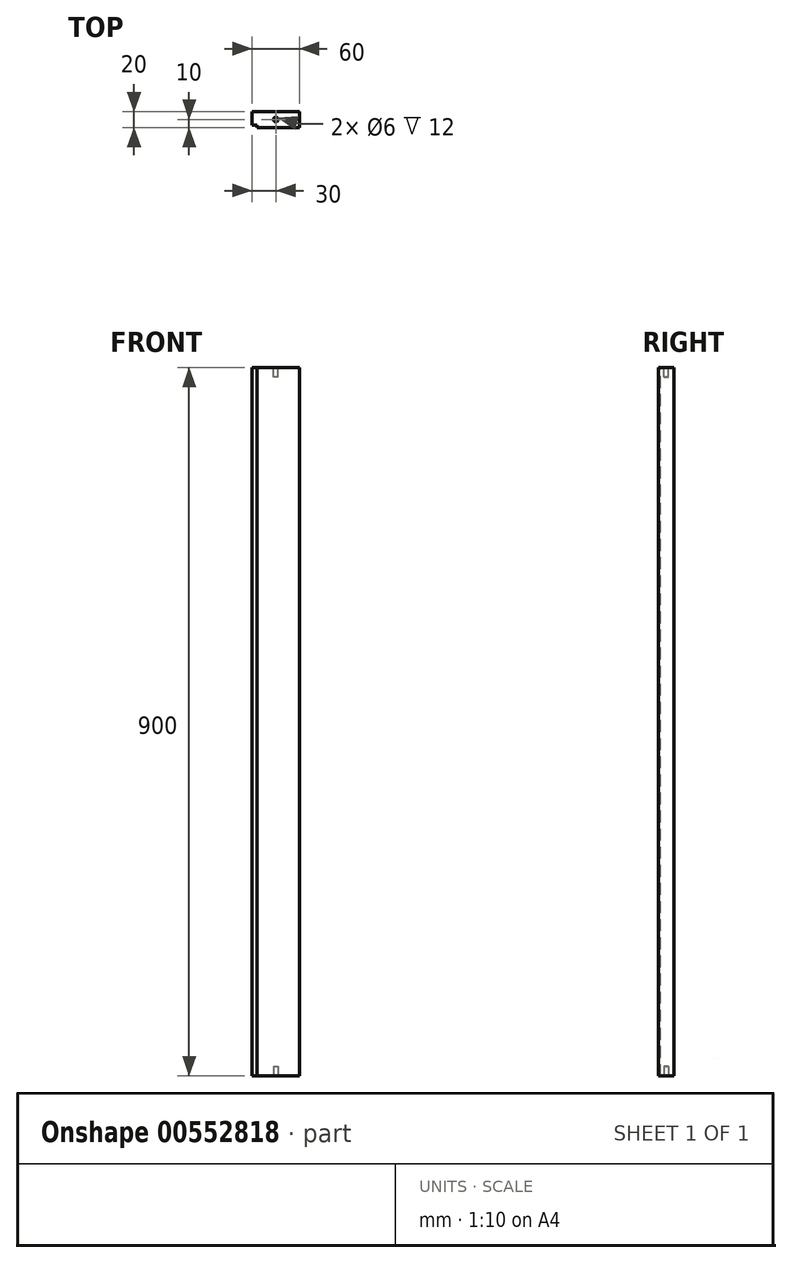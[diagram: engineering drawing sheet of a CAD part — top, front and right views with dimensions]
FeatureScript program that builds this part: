
annotation { "Feature Type Name" : "Feature", "Feature Type Description" : "" }
export const myFeature = defineFeature(function(context is Context, id is Id, definition is map)
    precondition{}
    {
        {
            var Q0;
            Q0=qCreatedBy(makeId("Top.planeOp"),FACE);
            var sketch = newSketch(context, id + "F0", { "sketchPlane" : qUnion([Q0])});
            skLineSegment(sketch, "E0.bottom", {"start": v(0, 0) * mm, "end": v(60, 0) * mm});
            skLineSegment(sketch, "E0.top", {"start": v(0, 20) * mm, "end": v(60, 20) * mm});
            skLineSegment(sketch, "E0.left", {"start": v(0, 0) * mm, "end": v(0, 20) * mm});
            skLineSegment(sketch, "E0.right", {"start": v(60, 0) * mm, "end": v(60, 20) * mm});
            skSolve(sketch);
        }
        {
            var Q0;
            Q0 = qSketchRegion(id + "F0", true);
            extrude(context, id + "F1", {"entities" : qUnion([Q0]), "depth" : 900 * mm, "offsetDistance" : 25 * mm});
        }
        {
            var Q0;
            Q0=makeQuery(id+"F1.opExtrude","CAP_FACE",FACE,{"disambiguationData":[OSD([sQuery(id+"F0.wireOp",EDGE,"E0.bottom"),sQuery(id+"F0.wireOp",EDGE,"E0.top"),sQuery(id+"F0.wireOp",EDGE,"E0.left"),sQuery(id+"F0.wireOp",EDGE,"E0.right")])],"isStart":false});
            var sketch = newSketch(context, id + "F2", { "sketchPlane" : qUnion([Q0])});
            skSolve(sketch);
        }
        {
            var Q0;
            Q0=makeQuery(id+"F1.opExtrude","CAP_FACE",FACE,{"disambiguationData":[OSD([sQuery(id+"F0.wireOp",EDGE,"E0.bottom"),sQuery(id+"F0.wireOp",EDGE,"E0.top"),sQuery(id+"F0.wireOp",EDGE,"E0.left"),sQuery(id+"F0.wireOp",EDGE,"E0.right")])],"isStart":true});
            var sketch = newSketch(context, id + "F3", { "sketchPlane" : qUnion([Q0])});
            skCircle(sketch, "E1", {"center": v(30, -10) * mm, "radius": 3 * mm});
            skPoint(sketch, "E1.centerSnap0", {"position": v(30, -20) * mm});
            skPoint(sketch, "E1.centerSnap1", {"position": v(60, -10) * mm});
            skSolve(sketch);
        }
        {
            var Q0;
            Q0=makeQuery(id+"F3.imprint","IMPRINT",FACE,{"disambiguationData":[TD([[makeQuery(id+"F3.imprint","IMPRINT",EDGE,{"derivedFrom":sQuery(id+"F3.wireOp",EDGE,"E1")}),1.0]])]});
            var Q1;
            Q1=sQuery(id+"F3.wireOp",EDGE,"E1");
            extrude(context, id + "F4", {"entities" : qUnion([Q0]), "operationType" : NewBodyOperationType.REMOVE, "surfaceEntities" : qUnion([Q1]), "oppositeDirection" : true, "depth" : 12 * mm, "offsetDistance" : 25 * mm});
        }
        {
            var Q0;
            Q0=makeQuery(id+"F2.imprint","IMPRINT",FACE,{"disambiguationData":[TD([[makeQuery(id+"F2.imprint","IMPRINT",EDGE,{"derivedFrom":makeQuery(id+"F1.opExtrude","CAP_EDGE",EDGE,{"disambiguationData":[OSD([sQuery(id+"F0.wireOp",EDGE,"E0.bottom")])],"isStart":false})}),1.0]])]});
            var sketch = newSketch(context, id + "F5", { "sketchPlane" : qUnion([Q0])});
            skCircle(sketch, "E2", {"center": v(30, 10) * mm, "radius": 3 * mm});
            skSolve(sketch);
        }
        {
            var Q0;
            Q0 = qSketchRegion(id + "F5", true);
            extrude(context, id + "F6", {"entities" : qUnion([Q0]), "operationType" : NewBodyOperationType.REMOVE, "oppositeDirection" : true, "depth" : 12 * mm, "offsetDistance" : 25 * mm});
        }
        {
            var Q0;
            Q0=makeQuery(id+"F2.imprint","IMPRINT",FACE,{"disambiguationData":[TD([[makeQuery(id+"F2.imprint","IMPRINT",EDGE,{"derivedFrom":makeQuery(id+"F1.opExtrude","CAP_EDGE",EDGE,{"disambiguationData":[OSD([sQuery(id+"F0.wireOp",EDGE,"E0.bottom")])],"isStart":false})}),1.0]])]});
            var sketch = newSketch(context, id + "F7", { "sketchPlane" : qUnion([Q0])});
            skLineSegment(sketch, "E3.bottom", {"start": v(0, 0) * mm, "end": v(6, 0) * mm});
            skLineSegment(sketch, "E3.top", {"start": v(0, 3) * mm, "end": v(6, 3) * mm});
            skLineSegment(sketch, "E3.left", {"start": v(0, 0) * mm, "end": v(0, 3) * mm});
            skLineSegment(sketch, "E3.right", {"start": v(6, 0) * mm, "end": v(6, 3) * mm});
            skSolve(sketch);
        }
        {
            var Q0;
            Q0=makeQuery(id+"F7.imprint","IMPRINT",FACE,{"disambiguationData":[TD([[makeQuery(id+"F7.imprint","IMPRINT",EDGE,{"derivedFrom":sQuery(id+"F7.wireOp",EDGE,"E3.bottom")}),1.0]])]});
            extrude(context, id + "F8", {"entities" : qUnion([Q0]), "operationType" : NewBodyOperationType.REMOVE, "oppositeDirection" : true, "depth" : 900 * mm, "offsetDistance" : 25 * mm});
        }
    });
